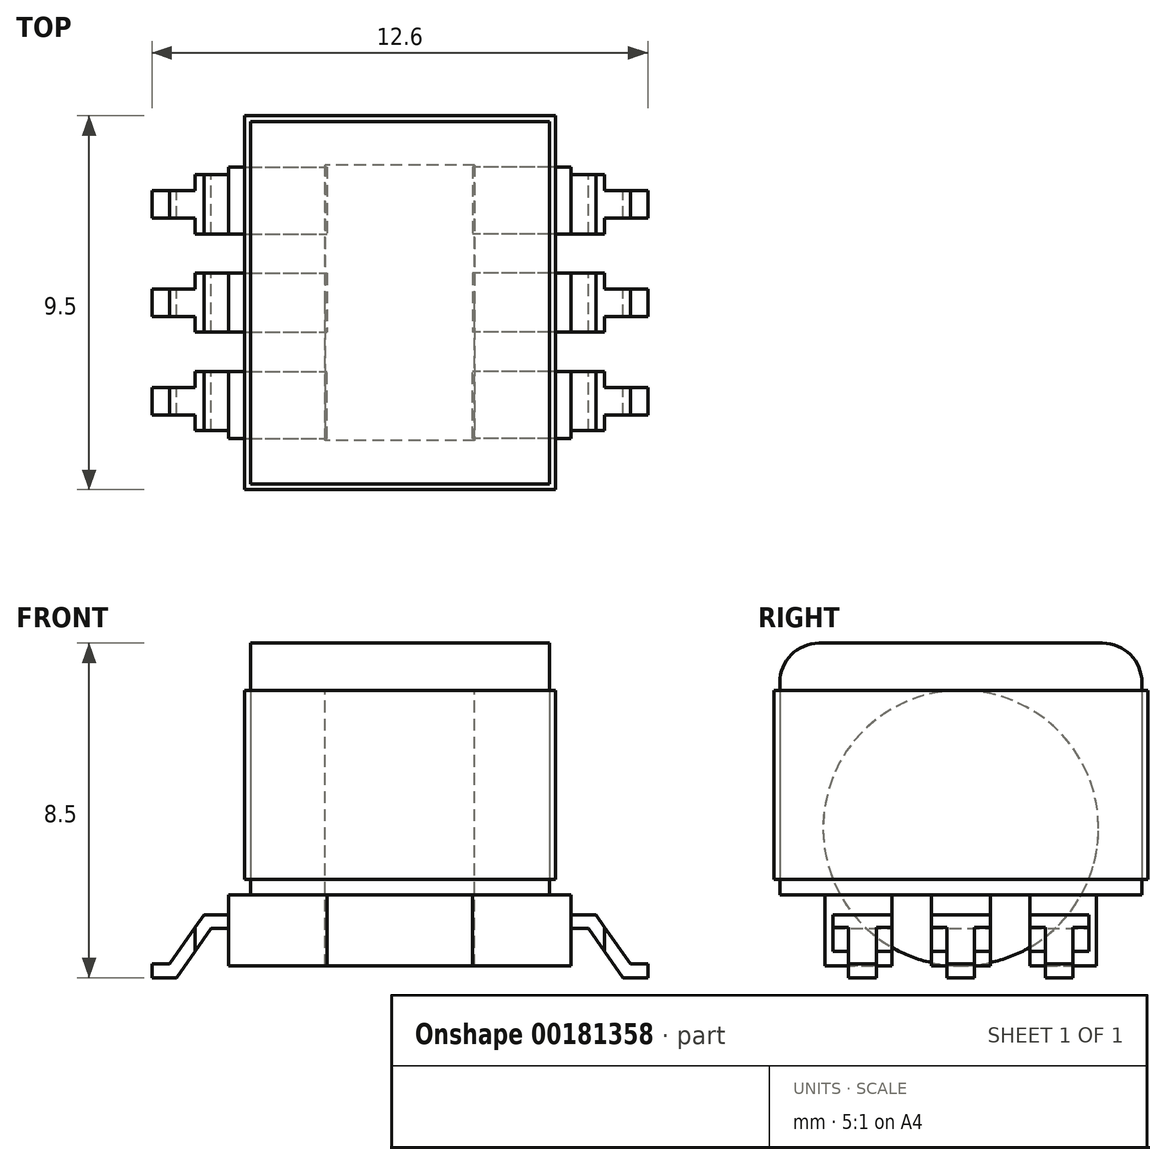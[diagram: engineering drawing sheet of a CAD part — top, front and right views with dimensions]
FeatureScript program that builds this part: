
annotation { "Feature Type Name" : "Feature", "Feature Type Description" : "" }
export const myFeature = defineFeature(function(context is Context, id is Id, definition is map)
    precondition{}
    {
        {
            var Q0;
            Q0=qCreatedBy(makeId("Top.planeOp"),FACE);
            var sketch = newSketch(context, id + "F0", { "sketchPlane" : qUnion([Q0])});
            skLineSegment(sketch, "E0.bottom", {"start": v(3.8, -4.6) * mm, "end": v(-3.8, -4.6) * mm});
            skLineSegment(sketch, "E0.top", {"start": v(3.8, 4.6) * mm, "end": v(-3.8, 4.6) * mm});
            skLineSegment(sketch, "E0.left", {"start": v(3.8, -4.6) * mm, "end": v(3.8, 4.6) * mm});
            skLineSegment(sketch, "E0.right", {"start": v(-3.8, -4.6) * mm, "end": v(-3.8, 4.6) * mm});
            skPoint(sketch, "E0.middle", {"position": v(0, 0) * mm});
            skSolve(sketch);
        }
        {
            var Q0;
            Q0 = qSketchRegion(id + "F0", true);
            extrude(context, id + "F1", {"entities" : qUnion([Q0]), "depth" : 6.4 * mm});
        }
        {
            var Q0;
            Q0=makeQuery(id+"F1.opExtrude","CAP_EDGE",EDGE,{"disambiguationData":[OSD([sQuery(id+"F0.wireOp",EDGE,"E0.top")])],"isStart":false});
            var Q1;
            Q1=makeQuery(id+"F1.opExtrude","CAP_EDGE",EDGE,{"disambiguationData":[OSD([sQuery(id+"F0.wireOp",EDGE,"E0.bottom")])],"isStart":false});
            fillet(context, id + "F2", {"entities" : qUnion([Q0, Q1]), "radius" : 1 * mm, "tangentPropagation" : true, "allowEdgeOverflow" : false});
        }
        {
            var Q0;
            Q0=qCreatedBy(makeId("Top.planeOp"),FACE);
            cPlane(context, id + "F3", {"entities" : qUnion([Q0]), "cplaneType" : CPlaneType.OFFSET, "offset" : 0.4 * mm, "width" : 150 * mm, "height" : 150 * mm});
        }
        {
            var Q0;
            Q0=qCreatedBy(id+"F3.planeOp",FACE);
            var sketch = newSketch(context, id + "F4", { "sketchPlane" : qUnion([Q0])});
            skLineSegment(sketch, "E1.bottom", {"start": v(3.95, 4.75) * mm, "end": v(-3.95, 4.75) * mm});
            skLineSegment(sketch, "E1.top", {"start": v(3.95, -4.75) * mm, "end": v(-3.95, -4.75) * mm});
            skLineSegment(sketch, "E1.left", {"start": v(3.95, 4.75) * mm, "end": v(3.95, -4.75) * mm});
            skLineSegment(sketch, "E1.right", {"start": v(-3.95, 4.75) * mm, "end": v(-3.95, -4.75) * mm});
            skLineSegment(sketch, "E2", {"start": v(3.8, 4.6) * mm, "end": v(3.8, 4.75) * mm, "construction": true});
            skLineSegment(sketch, "E3", {"start": v(3.8, 4.6) * mm, "end": v(3.95, 4.6) * mm, "construction": true});
            skLineSegment(sketch, "E4", {"start": v(-3.8, -4.75) * mm, "end": v(-3.8, -4.6) * mm, "construction": true});
            skLineSegment(sketch, "E5", {"start": v(-3.8, -4.6) * mm, "end": v(-3.95, -4.6) * mm, "construction": true});
            skSolve(sketch);
        }
        {
            var Q0;
            Q0 = qSketchRegion(id + "F4", true);
            extrude(context, id + "F5", {"entities" : qUnion([Q0]), "depth" : 4.8 * mm});
        }
        {
            var Q0;
            Q0=makeQuery(id+"F1.opExtrude","CAP_FACE",FACE,{"disambiguationData":[OSD([sQuery(id+"F0.wireOp",EDGE,"E0.bottom"),sQuery(id+"F0.wireOp",EDGE,"E0.top"),sQuery(id+"F0.wireOp",EDGE,"E0.left"),sQuery(id+"F0.wireOp",EDGE,"E0.right")])],"isStart":true});
            var sketch = newSketch(context, id + "F6", { "sketchPlane" : qUnion([Q0])});
            skLineSegment(sketch, "E6.bottom", {"start": v(4.35, -3.45) * mm, "end": v(1.85, -3.45) * mm});
            skLineSegment(sketch, "E6.top", {"start": v(4.35, -1.75) * mm, "end": v(1.85, -1.75) * mm});
            skLineSegment(sketch, "E6.right", {"start": v(1.85, -3.45) * mm, "end": v(1.85, -1.75) * mm});
            skLineSegment(sketch, "E7.bottom", {"start": v(4.35, -0.75) * mm, "end": v(1.85, -0.75) * mm});
            skLineSegment(sketch, "E7.top", {"start": v(4.35, 0.75) * mm, "end": v(1.85, 0.75) * mm});
            skLineSegment(sketch, "E7.right", {"start": v(1.85, -0.75) * mm, "end": v(1.85, 0.75) * mm});
            skLineSegment(sketch, "E8", {"start": v(4.35, 0) * mm, "end": v(0, 0) * mm, "construction": true});
            skLineSegment(sketch, "E9", {"start": v(0, 0) * mm, "end": v(0, -4.6) * mm, "construction": true});
            skLineSegment(sketch, "E10.MirrorCS", {"start": v(4.35, 3.45) * mm, "end": v(1.85, 3.45) * mm});
            skLineSegment(sketch, "E11.MirrorCS", {"start": v(4.35, 1.75) * mm, "end": v(1.85, 1.75) * mm});
            skLineSegment(sketch, "E12.MirrorCS", {"start": v(1.85, 3.45) * mm, "end": v(1.85, 1.75) * mm});
            skLineSegment(sketch, "E13.MirrorCS", {"start": v(-4.35, 3.45) * mm, "end": v(-1.85, 3.45) * mm});
            skLineSegment(sketch, "E14.MirrorCS", {"start": v(-4.35, 1.75) * mm, "end": v(-1.85, 1.75) * mm});
            skLineSegment(sketch, "E15.MirrorCS", {"start": v(-4.35, -0.75) * mm, "end": v(-1.85, -0.75) * mm});
            skLineSegment(sketch, "E16.MirrorCS", {"start": v(-1.85, -3.45) * mm, "end": v(-1.85, -1.75) * mm});
            skLineSegment(sketch, "E17.MirrorCS", {"start": v(-4.35, -3.45) * mm, "end": v(-4.35, -1.75) * mm});
            skLineSegment(sketch, "E18.MirrorCS", {"start": v(-4.35, 0.75) * mm, "end": v(-1.85, 0.75) * mm});
            skLineSegment(sketch, "E19.MirrorCS", {"start": v(-4.35, 3.45) * mm, "end": v(-4.35, 1.75) * mm});
            skLineSegment(sketch, "E20.MirrorCS", {"start": v(-4.35, -1.75) * mm, "end": v(-1.85, -1.75) * mm});
            skLineSegment(sketch, "E21.MirrorCS", {"start": v(-1.85, -0.75) * mm, "end": v(-1.85, 0.75) * mm});
            skLineSegment(sketch, "E22.MirrorCS", {"start": v(-1.85, 3.45) * mm, "end": v(-1.85, 1.75) * mm});
            skLineSegment(sketch, "E23.MirrorCS", {"start": v(-4.35, -0.75) * mm, "end": v(-4.35, 0.75) * mm});
            skLineSegment(sketch, "E24.MirrorCS", {"start": v(-4.35, -3.45) * mm, "end": v(-1.85, -3.45) * mm});
            skLineSegment(sketch, "E25", {"start": v(4.35, -1.75) * mm, "end": v(4.35, -3.45) * mm});
            skLineSegment(sketch, "E26", {"start": v(4.35, -0.75) * mm, "end": v(4.35, 0.75) * mm});
            skLineSegment(sketch, "E27", {"start": v(4.35, 1.75) * mm, "end": v(4.35, 3.45) * mm});
            skPoint(sketch, "E28", {"position": v(4.35, 0) * mm});
            skSolve(sketch);
        }
        {
            var Q0;
            Q0 = qSketchRegion(id + "F6", true);
            extrude(context, id + "F7", {"entities" : qUnion([Q0]), "operationType" : NewBodyOperationType.ADD, "depth" : 1.8 * mm});
        }
        {
            var Q0;
            Q0=qCreatedBy(makeId("Right.planeOp"),FACE);
            var sketch = newSketch(context, id + "F8", { "sketchPlane" : qUnion([Q0])});
            skCircle(sketch, "E29", {"center": v(0, 1.7) * mm, "radius": 3.5 * mm});
            skLineSegment(sketch, "E30", {"start": v(0, 0) * mm, "end": v(0, 1.7) * mm, "construction": true});
            skSolve(sketch);
        }
        {
            var Q0;
            Q0 = qSketchRegion(id + "F8", true);
            extrude(context, id + "F9", {"entities" : qUnion([Q0]), "endBound" : BoundingType.SYMMETRIC, "depth" : 3.8 * mm});
        }
        {
            var Q0;
            Q0=qCreatedBy(makeId("Front.planeOp"),FACE);
            var sketch = newSketch(context, id + "F10", { "sketchPlane" : qUnion([Q0])});
            skLineSegment(sketch, "E31", {"start": v(4.35, -0.5) * mm, "end": v(4.98, -0.5) * mm});
            skLineSegment(sketch, "E32", {"start": v(4.98, -0.5) * mm, "end": v(5.85, -1.75) * mm});
            skLineSegment(sketch, "E33", {"start": v(5.85, -1.75) * mm, "end": v(6.3, -1.75) * mm});
            skLineSegment(sketch, "E34", {"start": v(6.3, -1.75) * mm, "end": v(6.3, -2.1) * mm});
            skLineSegment(sketch, "E35.0", {"start": v(5.67, -2.1) * mm, "end": v(6.3, -2.1) * mm});
            skLineSegment(sketch, "E35.1", {"start": v(4.8, -0.85) * mm, "end": v(5.67, -2.1) * mm});
            skLineSegment(sketch, "E35.2", {"start": v(4.35, -0.85) * mm, "end": v(4.8, -0.85) * mm});
            skLineSegment(sketch, "E36", {"start": v(0, 0) * mm, "end": v(0, -1.8) * mm, "construction": true});
            skLineSegment(sketch, "E37.MirrorCS", {"start": v(-4.35, -0.85) * mm, "end": v(-4.8, -0.85) * mm});
            skLineSegment(sketch, "E38.MirrorCS", {"start": v(-4.8, -0.85) * mm, "end": v(-5.67, -2.1) * mm});
            skLineSegment(sketch, "E39.MirrorCS", {"start": v(-5.67, -2.1) * mm, "end": v(-6.3, -2.1) * mm});
            skLineSegment(sketch, "E40.MirrorCS", {"start": v(-6.3, -1.75) * mm, "end": v(-6.3, -2.1) * mm});
            skLineSegment(sketch, "E41.MirrorCS", {"start": v(-4.35, -0.5) * mm, "end": v(-4.98, -0.5) * mm});
            skLineSegment(sketch, "E42.MirrorCS", {"start": v(-4.98, -0.5) * mm, "end": v(-5.85, -1.75) * mm});
            skLineSegment(sketch, "E43.MirrorCS", {"start": v(-5.85, -1.75) * mm, "end": v(-6.3, -1.75) * mm});
            skLineSegment(sketch, "E44", {"start": v(-4.35, -0.5) * mm, "end": v(-4.35, -0.85) * mm});
            skLineSegment(sketch, "E45", {"start": v(4.35, -0.5) * mm, "end": v(4.35, -0.85) * mm});
            skSolve(sketch);
        }
        {
            var Q0;
            Q0 = qSketchRegion(id + "F10", true);
            extrude(context, id + "F11", {"entities" : qUnion([Q0]), "endBound" : BoundingType.SYMMETRIC, "depth" : 7 * mm});
        }
        {
            var Q0;
            Q0=qCreatedBy(makeId("Top.planeOp"),FACE);
            var sketch = newSketch(context, id + "F12", { "sketchPlane" : qUnion([Q0])});
            skLineSegment(sketch, "E46.bottom", {"start": v(-6.3, -3.5) * mm, "end": v(-4.35, -3.5) * mm});
            skLineSegment(sketch, "E46.top", {"start": v(-6.3, -3.25) * mm, "end": v(-4.35, -3.25) * mm});
            skLineSegment(sketch, "E46.left", {"start": v(-6.3, -3.5) * mm, "end": v(-6.3, -3.25) * mm});
            skLineSegment(sketch, "E46.right", {"start": v(-4.35, -3.5) * mm, "end": v(-4.35, -3.25) * mm});
            skLineSegment(sketch, "E47.bottom", {"start": v(-6.3, -1.75) * mm, "end": v(-4.35, -1.75) * mm});
            skLineSegment(sketch, "E47.top", {"start": v(-6.3, -0.75) * mm, "end": v(-4.35, -0.75) * mm});
            skLineSegment(sketch, "E47.left", {"start": v(-6.3, -1.75) * mm, "end": v(-6.3, -0.75) * mm});
            skLineSegment(sketch, "E47.right", {"start": v(-4.35, -1.75) * mm, "end": v(-4.35, -0.75) * mm});
            skLineSegment(sketch, "E48", {"start": v(0, 0) * mm, "end": v(-6.3, 0) * mm, "construction": true});
            skLineSegment(sketch, "E49.MirrorCS", {"start": v(-6.3, 3.5) * mm, "end": v(-4.35, 3.5) * mm});
            skLineSegment(sketch, "E50.MirrorCS", {"start": v(-6.3, 3.25) * mm, "end": v(-4.35, 3.25) * mm});
            skLineSegment(sketch, "E51.MirrorCS", {"start": v(-6.3, 3.5) * mm, "end": v(-6.3, 3.25) * mm});
            skLineSegment(sketch, "E52.MirrorCS", {"start": v(-4.35, 3.5) * mm, "end": v(-4.35, 3.25) * mm});
            skLineSegment(sketch, "E53.MirrorCS", {"start": v(-6.3, 1.75) * mm, "end": v(-4.35, 1.75) * mm});
            skLineSegment(sketch, "E54.MirrorCS", {"start": v(-4.35, 1.75) * mm, "end": v(-4.35, 0.75) * mm});
            skLineSegment(sketch, "E55.MirrorCS", {"start": v(-6.3, 1.75) * mm, "end": v(-6.3, 0.75) * mm});
            skLineSegment(sketch, "E56.MirrorCS", {"start": v(-6.3, 0.75) * mm, "end": v(-4.35, 0.75) * mm});
            skLineSegment(sketch, "E57", {"start": v(-6.3, -2.5) * mm, "end": v(-4.35, -2.5) * mm, "construction": true});
            skLineSegment(sketch, "E58", {"start": v(0, 0) * mm, "end": v(0, -3.6) * mm, "construction": true});
            skLineSegment(sketch, "E59.MirrorCS", {"start": v(4.35, -3.5) * mm, "end": v(4.35, -3.25) * mm});
            skLineSegment(sketch, "E60.MirrorCS", {"start": v(4.35, 3.5) * mm, "end": v(4.35, 3.25) * mm});
            skLineSegment(sketch, "E61.MirrorCS", {"start": v(6.3, 3.5) * mm, "end": v(6.3, 3.25) * mm});
            skLineSegment(sketch, "E62.MirrorCS", {"start": v(6.3, -3.5) * mm, "end": v(6.3, -3.25) * mm});
            skLineSegment(sketch, "E63.MirrorCS", {"start": v(4.35, 1.75) * mm, "end": v(4.35, 0.75) * mm});
            skLineSegment(sketch, "E64.MirrorCS", {"start": v(6.3, -2.5) * mm, "end": v(4.35, -2.5) * mm, "construction": true});
            skLineSegment(sketch, "E65.MirrorCS", {"start": v(0, 0) * mm, "end": v(6.3, 0) * mm, "construction": true});
            skLineSegment(sketch, "E66.MirrorCS", {"start": v(6.3, -3.25) * mm, "end": v(4.35, -3.25) * mm});
            skLineSegment(sketch, "E67.MirrorCS", {"start": v(6.3, -0.75) * mm, "end": v(4.35, -0.75) * mm});
            skLineSegment(sketch, "E68.MirrorCS", {"start": v(6.3, -3.5) * mm, "end": v(4.35, -3.5) * mm});
            skLineSegment(sketch, "E69.MirrorCS", {"start": v(6.3, -1.75) * mm, "end": v(6.3, -0.75) * mm});
            skLineSegment(sketch, "E70.MirrorCS", {"start": v(6.3, -1.75) * mm, "end": v(4.35, -1.75) * mm});
            skLineSegment(sketch, "E71.MirrorCS", {"start": v(6.3, 0.75) * mm, "end": v(4.35, 0.75) * mm});
            skLineSegment(sketch, "E72.MirrorCS", {"start": v(6.3, 1.75) * mm, "end": v(4.35, 1.75) * mm});
            skLineSegment(sketch, "E73.MirrorCS", {"start": v(6.3, 3.25) * mm, "end": v(4.35, 3.25) * mm});
            skLineSegment(sketch, "E74.MirrorCS", {"start": v(6.3, 3.5) * mm, "end": v(4.35, 3.5) * mm});
            skLineSegment(sketch, "E75.MirrorCS", {"start": v(6.3, 1.75) * mm, "end": v(6.3, 0.75) * mm});
            skLineSegment(sketch, "E76.MirrorCS", {"start": v(4.35, -1.75) * mm, "end": v(4.35, -0.75) * mm});
            skSolve(sketch);
        }
        {
            var Q0;
            Q0 = qSketchRegion(id + "F12", true);
            extrude(context, id + "F13", {"entities" : qUnion([Q0]), "operationType" : NewBodyOperationType.REMOVE, "endBound" : BoundingType.THROUGH_ALL, "oppositeDirection" : true, "depth" : 25 * mm});
        }
        {
            var Q0;
            Q0=qCreatedBy(makeId("Top.planeOp"),FACE);
            var sketch = newSketch(context, id + "F14", { "sketchPlane" : qUnion([Q0])});
            skLineSegment(sketch, "E77", {"start": v(-6.3, -3.25) * mm, "end": v(-6.3, 3.25) * mm, "construction": true});
            skLineSegment(sketch, "E78.bottom", {"start": v(-6.3, -2.15) * mm, "end": v(-5.2, -2.15) * mm});
            skLineSegment(sketch, "E78.top", {"start": v(-6.3, -0.35) * mm, "end": v(-5.2, -0.35) * mm});
            skLineSegment(sketch, "E78.left", {"start": v(-6.3, -2.15) * mm, "end": v(-6.3, -0.35) * mm});
            skLineSegment(sketch, "E78.right", {"start": v(-5.2, -2.15) * mm, "end": v(-5.2, -0.35) * mm});
            skLineSegment(sketch, "E79.bottom", {"start": v(-6.3, 0.35) * mm, "end": v(-5.2, 0.35) * mm});
            skLineSegment(sketch, "E79.top", {"start": v(-6.3, 2.15) * mm, "end": v(-5.2, 2.15) * mm});
            skLineSegment(sketch, "E79.left", {"start": v(-6.3, 0.35) * mm, "end": v(-6.3, 2.15) * mm});
            skLineSegment(sketch, "E79.right", {"start": v(-5.2, 0.35) * mm, "end": v(-5.2, 2.15) * mm});
            skLineSegment(sketch, "E80.bottom", {"start": v(-6.3, -2.85) * mm, "end": v(-5.2, -2.85) * mm});
            skLineSegment(sketch, "E80.top", {"start": v(-6.3, -4.75) * mm, "end": v(-5.2, -4.75) * mm});
            skLineSegment(sketch, "E80.left", {"start": v(-6.3, -2.85) * mm, "end": v(-6.3, -4.75) * mm});
            skLineSegment(sketch, "E80.right", {"start": v(-5.2, -2.85) * mm, "end": v(-5.2, -4.75) * mm});
            skLineSegment(sketch, "E81.bottom", {"start": v(-6.3, 2.85) * mm, "end": v(-5.2, 2.85) * mm});
            skLineSegment(sketch, "E81.top", {"start": v(-6.3, 4.75) * mm, "end": v(-5.2, 4.75) * mm});
            skLineSegment(sketch, "E81.left", {"start": v(-6.3, 2.85) * mm, "end": v(-6.3, 4.75) * mm});
            skLineSegment(sketch, "E81.right", {"start": v(-5.2, 2.85) * mm, "end": v(-5.2, 4.75) * mm});
            skLineSegment(sketch, "E82", {"start": v(-5.2, -1.25) * mm, "end": v(-6.3, -1.25) * mm, "construction": true});
            skLineSegment(sketch, "E83", {"start": v(-5.2, 1.25) * mm, "end": v(-6.3, 1.25) * mm, "construction": true});
            skLineSegment(sketch, "E84", {"start": v(-6.3, 0) * mm, "end": v(-4.6, 0) * mm, "construction": true});
            skPoint(sketch, "E84.endSnap0", {"position": v(-6.3, 0) * mm});
            skLineSegment(sketch, "E85", {"start": v(-3.95, -2.5) * mm, "end": v(-6.3, -2.5) * mm, "construction": true});
            skLineSegment(sketch, "E86", {"start": v(0, 0) * mm, "end": v(0, -4.75) * mm, "construction": true});
            skLineSegment(sketch, "E87.MirrorCS", {"start": v(6.3, -2.15) * mm, "end": v(6.3, -0.35) * mm});
            skLineSegment(sketch, "E88.MirrorCS", {"start": v(6.3, 0.35) * mm, "end": v(6.3, 2.15) * mm});
            skLineSegment(sketch, "E89.MirrorCS", {"start": v(6.3, 2.85) * mm, "end": v(5.2, 2.85) * mm});
            skLineSegment(sketch, "E90.MirrorCS", {"start": v(6.3, 4.75) * mm, "end": v(5.2, 4.75) * mm});
            skLineSegment(sketch, "E91.MirrorCS", {"start": v(6.3, 2.85) * mm, "end": v(6.3, 4.75) * mm});
            skLineSegment(sketch, "E92.MirrorCS", {"start": v(6.3, -2.15) * mm, "end": v(5.2, -2.15) * mm});
            skLineSegment(sketch, "E93.MirrorCS", {"start": v(6.3, -3.25) * mm, "end": v(6.3, 3.25) * mm, "construction": true});
            skLineSegment(sketch, "E94.MirrorCS", {"start": v(5.2, -1.25) * mm, "end": v(6.3, -1.25) * mm, "construction": true});
            skLineSegment(sketch, "E95.MirrorCS", {"start": v(6.3, 0) * mm, "end": v(4.6, 0) * mm, "construction": true});
            skLineSegment(sketch, "E96.MirrorCS", {"start": v(6.3, -0.35) * mm, "end": v(5.2, -0.35) * mm});
            skLineSegment(sketch, "E97.MirrorCS", {"start": v(5.2, -2.15) * mm, "end": v(5.2, -0.35) * mm});
            skLineSegment(sketch, "E98.MirrorCS", {"start": v(6.3, 0.35) * mm, "end": v(5.2, 0.35) * mm});
            skLineSegment(sketch, "E99.MirrorCS", {"start": v(6.3, 2.15) * mm, "end": v(5.2, 2.15) * mm});
            skLineSegment(sketch, "E100.MirrorCS", {"start": v(5.2, 1.25) * mm, "end": v(6.3, 1.25) * mm, "construction": true});
            skLineSegment(sketch, "E101.MirrorCS", {"start": v(3.95, -2.5) * mm, "end": v(6.3, -2.5) * mm, "construction": true});
            skLineSegment(sketch, "E102.MirrorCS", {"start": v(6.3, -4.75) * mm, "end": v(5.2, -4.75) * mm});
            skLineSegment(sketch, "E103.MirrorCS", {"start": v(6.3, -2.85) * mm, "end": v(6.3, -4.75) * mm});
            skLineSegment(sketch, "E104.MirrorCS", {"start": v(6.3, -2.85) * mm, "end": v(5.2, -2.85) * mm});
            skLineSegment(sketch, "E105.MirrorCS", {"start": v(5.2, -2.85) * mm, "end": v(5.2, -4.75) * mm});
            skPoint(sketch, "E106.MirrorP", {"position": v(6.3, 0) * mm});
            skLineSegment(sketch, "E107.MirrorCS", {"start": v(5.2, 0.35) * mm, "end": v(5.2, 2.15) * mm});
            skLineSegment(sketch, "E108.MirrorCS", {"start": v(5.2, 2.85) * mm, "end": v(5.2, 4.75) * mm});
            skSolve(sketch);
        }
        {
            var Q0;
            Q0 = qSketchRegion(id + "F14", true);
            extrude(context, id + "F15", {"entities" : qUnion([Q0]), "operationType" : NewBodyOperationType.REMOVE, "oppositeDirection" : true, "depth" : 25 * mm});
        }
    });
